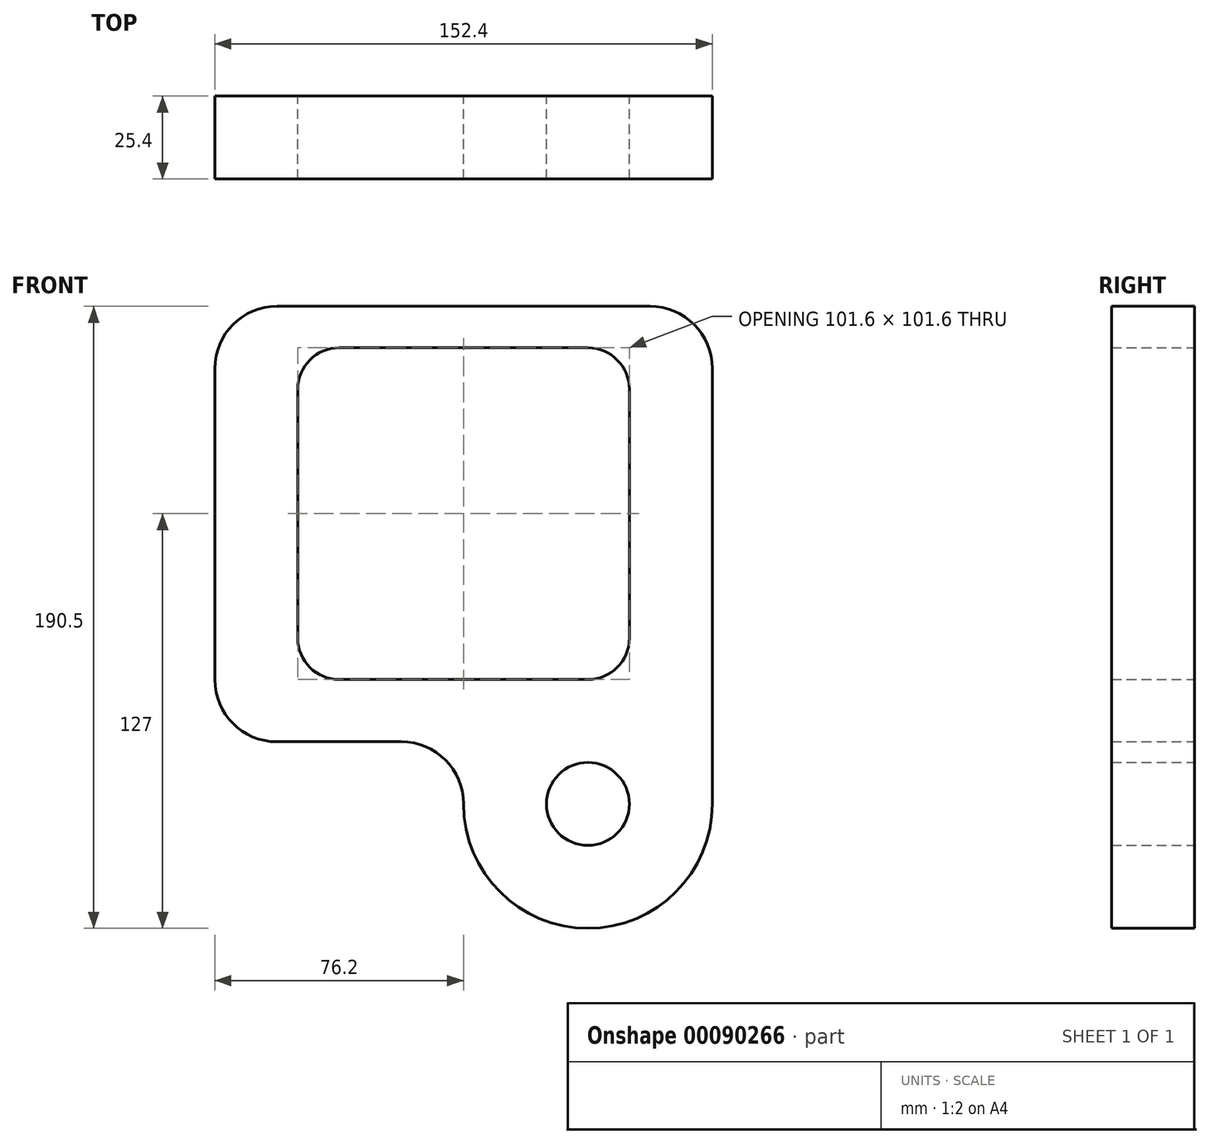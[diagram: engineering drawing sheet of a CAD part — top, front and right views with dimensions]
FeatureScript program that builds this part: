
annotation { "Feature Type Name" : "Feature", "Feature Type Description" : "" }
export const myFeature = defineFeature(function(context is Context, id is Id, definition is map)
    precondition{}
    {
        {
            var Q0;
            Q0=qCreatedBy(makeId("Front.planeOp"),FACE);
            var sketch = newSketch(context, id + "F0", { "sketchPlane" : qUnion([Q0])});
            skLineSegment(sketch, "E0", {"start": v(19.05, 0) * mm, "end": v(133.35, 0) * mm});
            skLineSegment(sketch, "E1", {"start": v(152.4, -19.05) * mm, "end": v(152.4, -152.4) * mm});
            skCircle(sketch, "E2", {"center": v(114.3, -152.4) * mm, "radius": 12.7 * mm});
            skPoint(sketch, "E3.visualSharp", {"position": v(0, 0) * mm});
            skArc(sketch, "E3.filletArc", {"start": v(19.05, 0) * mm, "mid": v(5.58, -5.58) * mm, "end": v(0, -19.05) * mm});
            skPoint(sketch, "E4.visualSharp", {"position": v(152.4, 0) * mm});
            skArc(sketch, "E4.filletArc", {"start": v(152.4, -19.05) * mm, "mid": v(146.82, -5.58) * mm, "end": v(133.35, 0) * mm});
            skLineSegment(sketch, "E5", {"start": v(76.2, 0) * mm, "end": v(76.2, -114.3) * mm, "construction": true});
            skLineSegment(sketch, "E6.top", {"start": v(38.1, -114.3) * mm, "end": v(114.3, -114.3) * mm});
            skLineSegment(sketch, "E6.left", {"start": v(25.4, -25.4) * mm, "end": v(25.4, -101.6) * mm});
            skLineSegment(sketch, "E6.right", {"start": v(127, -25.4) * mm, "end": v(127, -101.6) * mm});
            skPoint(sketch, "E7", {"position": v(76.2, -114.3) * mm});
            skPoint(sketch, "E8.visualSharp", {"position": v(25.4, -114.3) * mm});
            skArc(sketch, "E8.filletArc", {"start": v(25.4, -101.6) * mm, "mid": v(29.12, -110.58) * mm, "end": v(38.1, -114.3) * mm});
            skPoint(sketch, "E9.visualSharp", {"position": v(127, -114.3) * mm});
            skArc(sketch, "E9.filletArc", {"start": v(114.3, -114.3) * mm, "mid": v(123.28, -110.58) * mm, "end": v(127, -101.6) * mm});
            skLineSegment(sketch, "E10", {"start": v(38.1, -12.7) * mm, "end": v(114.3, -12.7) * mm});
            skPoint(sketch, "E11.visualSharp", {"position": v(25.4, -12.7) * mm});
            skArc(sketch, "E11.filletArc", {"start": v(38.1, -12.7) * mm, "mid": v(29.12, -16.42) * mm, "end": v(25.4, -25.4) * mm});
            skPoint(sketch, "E12.visualSharp", {"position": v(127, -12.7) * mm});
            skArc(sketch, "E12.filletArc", {"start": v(127, -25.4) * mm, "mid": v(123.28, -16.42) * mm, "end": v(114.3, -12.7) * mm});
            skArc(sketch, "E13", {"start": v(76.2, -152.4) * mm, "mid": v(114.3, -190.5) * mm, "end": v(152.4, -152.4) * mm});
            skLineSegment(sketch, "E14", {"start": v(0, -19.05) * mm, "end": v(0, -114.3) * mm});
            skLineSegment(sketch, "E15", {"start": v(19.05, -133.35) * mm, "end": v(57.15, -133.35) * mm});
            skPoint(sketch, "E16.visualSharp", {"position": v(76.2, -133.35) * mm});
            skArc(sketch, "E16.filletArc", {"start": v(76.2, -152.4) * mm, "mid": v(70.62, -138.93) * mm, "end": v(57.15, -133.35) * mm});
            skPoint(sketch, "E17.visualSharp", {"position": v(0, -133.35) * mm});
            skArc(sketch, "E17.filletArc", {"start": v(0, -114.3) * mm, "mid": v(5.58, -127.77) * mm, "end": v(19.05, -133.35) * mm});
            skSolve(sketch);
        }
        {
            var Q0;
            Q0=makeQuery(id+"F0.imprint","IMPRINT",FACE,{"disambiguationData":[TD([[makeQuery(id+"F0.imprint","IMPRINT",EDGE,{"derivedFrom":sQuery(id+"F0.wireOp",EDGE,"E0")}),-1.0]])]});
            extrude(context, id + "F1", {"entities" : qUnion([Q0]), "depth" : 25.4 * mm});
        }
    });
